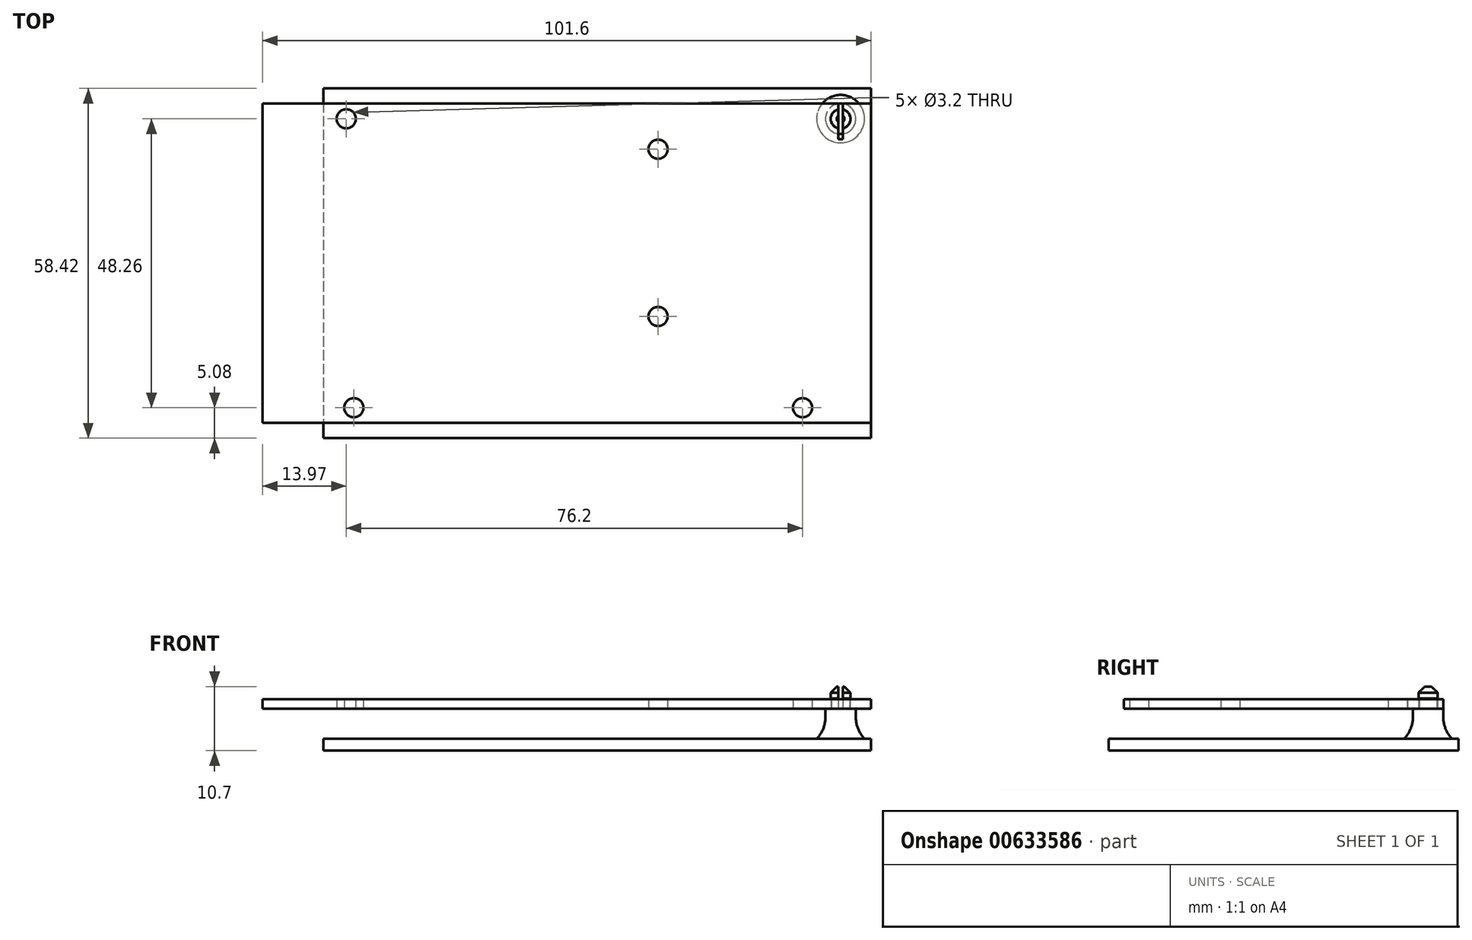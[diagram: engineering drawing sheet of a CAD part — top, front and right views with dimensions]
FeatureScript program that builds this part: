
annotation { "Feature Type Name" : "Feature", "Feature Type Description" : "" }
export const myFeature = defineFeature(function(context is Context, id is Id, definition is map)
    precondition{}
    {
        {
            var Q0;
            Q0=qCreatedBy(makeId("Top.planeOp"),FACE);
            var sketch = newSketch(context, id + "F0", { "sketchPlane" : qUnion([Q0])});
            skLineSegment(sketch, "E0.bottom", {"start": v(-50.8, -26.67) * mm, "end": v(50.8, -26.67) * mm});
            skLineSegment(sketch, "E0.top", {"start": v(-50.8, 26.67) * mm, "end": v(50.8, 26.67) * mm});
            skLineSegment(sketch, "E0.left", {"start": v(-50.8, -26.67) * mm, "end": v(-50.8, 26.67) * mm});
            skLineSegment(sketch, "E0.right", {"start": v(50.8, -26.67) * mm, "end": v(50.8, 26.67) * mm});
            skCircle(sketch, "E1", {"center": v(45.72, 24.13) * mm, "radius": 1.6 * mm});
            skCircle(sketch, "E2", {"center": v(15.24, 19.05) * mm, "radius": 1.6 * mm});
            skCircle(sketch, "E3", {"center": v(15.24, -8.9) * mm, "radius": 1.6 * mm});
            skCircle(sketch, "E4", {"center": v(39.37, -24.13) * mm, "radius": 1.6 * mm});
            skCircle(sketch, "E5", {"center": v(-35.56, -24.13) * mm, "radius": 1.6 * mm});
            skCircle(sketch, "E6", {"center": v(-36.83, 24.13) * mm, "radius": 1.6 * mm});
            skLineSegment(sketch, "E7", {"start": v(-36.83, 24.13) * mm, "end": v(45.72, 24.13) * mm, "construction": true});
            skLineSegment(sketch, "E8", {"start": v(-35.56, -24.13) * mm, "end": v(39.37, -24.13) * mm, "construction": true});
            skLineSegment(sketch, "E9", {"start": v(15.24, 19.05) * mm, "end": v(15.24, -8.9) * mm, "construction": true});
            skSolve(sketch);
        }
        {
            var Q0;
            Q0=qSketchRegion(id+"F0",true);
            extrude(context, id + "F1", {"entities" : qUnion([Q0]), "depth" : 1.6 * mm});
        }
        {
            var Q0;
            Q0=makeQuery(id+"F1.opExtrude","CAP_FACE",FACE,{"disambiguationData":[OSD([sQuery(id+"F0.wireOp",EDGE,"E0.bottom"),sQuery(id+"F0.wireOp",EDGE,"E0.top"),sQuery(id+"F0.wireOp",EDGE,"E0.left"),sQuery(id+"F0.wireOp",EDGE,"E0.right"),sQuery(id+"F0.wireOp",EDGE,"E1"),sQuery(id+"F0.wireOp",EDGE,"E2"),sQuery(id+"F0.wireOp",EDGE,"E3"),sQuery(id+"F0.wireOp",EDGE,"E4"),sQuery(id+"F0.wireOp",EDGE,"E5"),sQuery(id+"F0.wireOp",EDGE,"E6")])],"isStart":true});
            var sketch = newSketch(context, id + "F2", { "sketchPlane" : qUnion([Q0])});
            skCircle(sketch, "E10", {"center": v(45.72, -24.13) * mm, "radius": 2.54 * mm});
            skSolve(sketch);
        }
        {
            var Q0;
            Q0=qSketchRegion(id+"F2",true);
            extrude(context, id + "F3", {"entities" : qUnion([Q0]), "depth" : 5 * mm});
        }
        {
            var Q0;
            Q0=makeQuery(id+"F3.opExtrude","CAP_FACE",FACE,{"disambiguationData":[OSD([sQuery(id+"F2.wireOp",EDGE,"E10")])],"isStart":true});
            var sketch = newSketch(context, id + "F4", { "sketchPlane" : qUnion([Q0])});
            skCircle(sketch, "E11", {"center": v(45.72, 24.13) * mm, "radius": 1.5 * mm});
            skSolve(sketch);
        }
        {
            var Q0;
            Q0=qSketchRegion(id+"F4",true);
            extrude(context, id + "F5", {"entities" : qUnion([Q0]), "operationType" : NewBodyOperationType.ADD, "depth" : 3.7 * mm});
        }
        {
            var Q0;
            Q0=makeQuery(id+"F5.opExtrude","CAP_FACE",FACE,{"disambiguationData":[OSD([sQuery(id+"F4.wireOp",EDGE,"E11")])],"isStart":false});
            var sketch = newSketch(context, id + "F6", { "sketchPlane" : qUnion([Q0])});
            skCircle(sketch, "E12", {"center": v(45.72, 24.13) * mm, "radius": 1.65 * mm});
            skSolve(sketch);
        }
        {
            var Q0;
            Q0=makeQuery(id+"F6.imprint","IMPRINT",FACE,{"disambiguationData":[TD([[makeQuery(id+"F6.imprint","IMPRINT",EDGE,{"derivedFrom":sQuery(id+"F6.wireOp",EDGE,"E12")}),1.0]])]});
            extrude(context, id + "F7", {"entities" : qUnion([Q0]), "operationType" : NewBodyOperationType.ADD, "oppositeDirection" : true, "depth" : (3.7 - 1.7) * mm});
        }
        {
            var Q0;
            Q0=makeQuery(id+"F7.opExtrude","CAP_EDGE",EDGE,{"disambiguationData":[OSD([sQuery(id+"F6.wireOp",EDGE,"E12")])],"isStart":true});
            chamfer(context, id + "F8", {"entities" : qUnion([Q0]), "width" : (1) * mm, "tangentPropagation" : true});
        }
        {
            var Q0;
            {var subQ0=sQuery(id+"F4.wireOp",EDGE,"E11");Q0=makeQuery(id+"F7.boolean.opBoolean","MERGE",FACE,{"derivedFrom":[makeQuery(id+"F5.opExtrude","CAP_FACE",FACE,{"disambiguationData":[OSD([subQ0])],"isStart":false}),makeQuery(id+"F7.opExtrude","CAP_FACE",FACE,{"disambiguationData":[OSD([subQ0,sQuery(id+"F6.wireOp",EDGE,"E12")])],"isStart":true})]});}
            var sketch = newSketch(context, id + "F9", { "sketchPlane" : qUnion([Q0])});
            skLineSegment(sketch, "E13.bottom", {"start": v(45.32, 27.5) * mm, "end": v(46.12, 27.5) * mm});
            skLineSegment(sketch, "E13.top", {"start": v(45.32, 20.75) * mm, "end": v(46.12, 20.75) * mm});
            skLineSegment(sketch, "E13.left", {"start": v(45.32, 27.5) * mm, "end": v(45.32, 20.75) * mm});
            skLineSegment(sketch, "E13.right", {"start": v(46.12, 27.5) * mm, "end": v(46.12, 20.75) * mm});
            skPoint(sketch, "E13.middle", {"position": v(45.72, 24.13) * mm});
            skSolve(sketch);
        }
        {
            var Q0;
            {var subQ0=sQuery(id+"F9.wireOp",EDGE,"E13.left");var subQ1=sQuery(id+"F6.wireOp",EDGE,"E12");var subQ2=sQuery(id+"F4.wireOp",EDGE,"E11");var subQ3=makeQuery(id+"F8.opChamfer","BLEND_EDGE",EDGE,{"blendedFrom":[makeQuery(id+"F7.opExtrude","CAP_EDGE",EDGE,{"disambiguationData":[OSD([subQ1])],"isStart":true}),makeQuery(id+"F7.boolean.opBoolean","MERGE",FACE,{"derivedFrom":[makeQuery(id+"F5.opExtrude","CAP_FACE",FACE,{"disambiguationData":[OSD([subQ2])],"isStart":false}),makeQuery(id+"F7.opExtrude","CAP_FACE",FACE,{"disambiguationData":[OSD([subQ2,subQ1])],"isStart":true})]})],"blendedInto":[makeQuery(id+"F7.boolean.opBoolean","MERGE",FACE,{"derivedFrom":[makeQuery(id+"F5.opExtrude","CAP_FACE",FACE,{"disambiguationData":[OSD([subQ2])],"isStart":false}),makeQuery(id+"F7.opExtrude","CAP_FACE",FACE,{"disambiguationData":[OSD([subQ2,subQ1])],"isStart":true})]})]});var subQ4=makeQuery(id+"F9.imprint","INTERSECT",VERTEX,{"disambiguationData":[OD(0.0)],"derivedFrom":[subQ3,subQ0]});Q0=makeQuery(id+"F9.imprint","IMPRINT",FACE,{"disambiguationData":[TD([[makeQuery(id+"F9.imprint","IMPRINT",EDGE,{"disambiguationData":[TD([[subQ4,-1.0]])],"derivedFrom":subQ0}),1.0]])]});}
            var Q1;
            {var subQ0=sQuery(id+"F9.wireOp",EDGE,"E13.top");Q1=makeQuery(id+"F9.imprint","IMPRINT",FACE,{"disambiguationData":[TD([[makeQuery(id+"F9.imprint","IMPRINT",EDGE,{"derivedFrom":subQ0}),1.0]])]});}
            var Q2;
            {var subQ0=sQuery(id+"F9.wireOp",EDGE,"E13.bottom");Q2=makeQuery(id+"F9.imprint","IMPRINT",FACE,{"disambiguationData":[TD([[makeQuery(id+"F9.imprint","IMPRINT",EDGE,{"derivedFrom":subQ0}),-1.0]])]});}
            extrude(context, id + "F10", {"entities" : qUnion([Q0, Q1, Q2]), "operationType" : NewBodyOperationType.REMOVE, "oppositeDirection" : true, "depth" : 3.7 * mm});
        }
        {
            var Q0;
            Q0=makeQuery(id+"F3.opExtrude","CAP_FACE",FACE,{"disambiguationData":[OSD([sQuery(id+"F2.wireOp",EDGE,"E10")])],"isStart":false});
            var sketch = newSketch(context, id + "F11", { "sketchPlane" : qUnion([Q0])});
            skLineSegment(sketch, "E14.bottom", {"start": v(50.8, -29.2) * mm, "end": v(-40.64, -29.2) * mm});
            skLineSegment(sketch, "E14.top", {"start": v(50.8, 29.21) * mm, "end": v(-40.64, 29.21) * mm});
            skLineSegment(sketch, "E14.left", {"start": v(50.8, -29.2) * mm, "end": v(50.8, 29.21) * mm});
            skLineSegment(sketch, "E14.right", {"start": v(-40.64, -29.2) * mm, "end": v(-40.64, 29.21) * mm});
            skCircle(sketch, "E15", {"center": v(45.72, -24.13) * mm, "radius": 5.08 * mm, "construction": true});
            skCircle(sketch, "E16", {"center": v(-35.56, 24.13) * mm, "radius": 5.08 * mm, "construction": true});
            skSolve(sketch);
        }
        {
            var Q0;
            Q0=qSketchRegion(id+"F11",true);
            extrude(context, id + "F12", {"entities" : qUnion([Q0]), "depth" : 2 * mm});
        }
        {
            var Q0;
            Q0=makeQuery(id+"F3.opExtrude","CAP_FACE",FACE,{"disambiguationData":[OSD([sQuery(id+"F2.wireOp",EDGE,"E10")])],"isStart":false});
            var sketch = newSketch(context, id + "F13", { "sketchPlane" : qUnion([Q0])});
            skCircle(sketch, "E17", {"center": v(45.72, -24.13) * mm, "radius": 4 * mm});
            skSolve(sketch);
        }
        {
            var Q0;
            Q0=qSketchRegion(id+"F13",true);
            var Q1;
            Q1=sQuery(id+"F13.wireOp",EDGE,"E17");
            extrude(context, id + "F14", {"entities" : qUnion([Q0]), "operationType" : NewBodyOperationType.ADD, "surfaceEntities" : qUnion([Q1]), "oppositeDirection" : true, "depth" : 0.01 * mm});
        }
        {
            var Q0;
            Q0=makeQuery(id+"F14.boolean.opBoolean","INTERSECT",EDGE,{"derivedFrom":[makeQuery(id+"F3.opExtrude","SWEPT_FACE",FACE,{"disambiguationData":[OSD([sQuery(id+"F2.wireOp",EDGE,"E10")])]}),makeQuery(id+"F14.opExtrude","CAP_FACE",FACE,{"disambiguationData":[OSD([sQuery(id+"F13.wireOp",EDGE,"E17")])],"isStart":false})]});
            fillet(context, id + "F15", {"entities" : qUnion([Q0]), "radius" : 5 * mm, "tangentPropagation" : true, "allowEdgeOverflow" : false});
        }
    });
